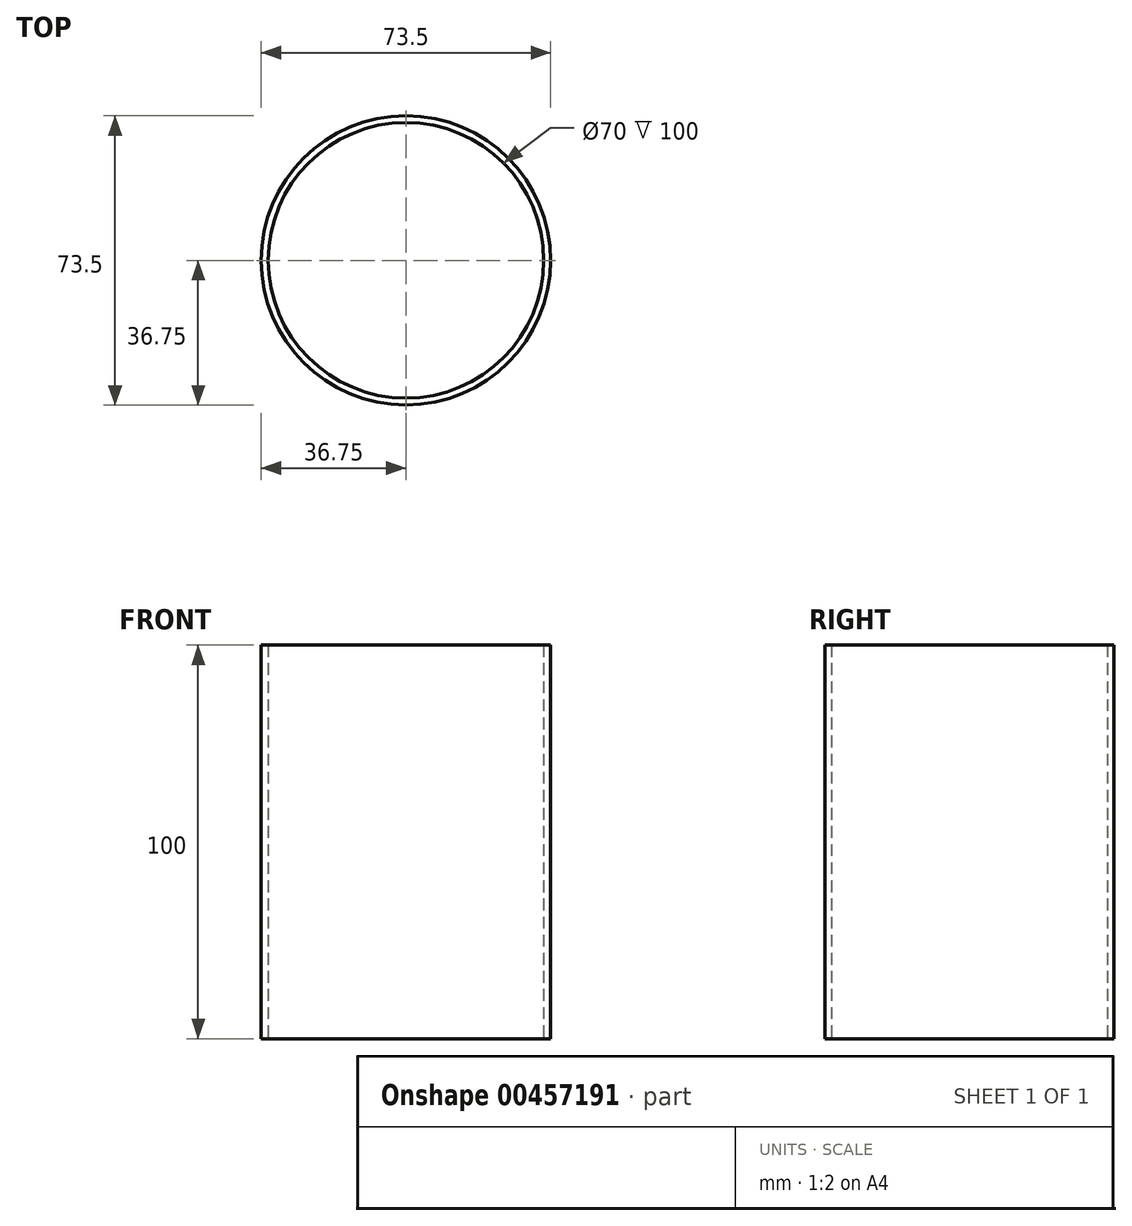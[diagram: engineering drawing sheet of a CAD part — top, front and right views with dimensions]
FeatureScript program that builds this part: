
annotation { "Feature Type Name" : "Feature", "Feature Type Description" : "" }
export const myFeature = defineFeature(function(context is Context, id is Id, definition is map)
    precondition{}
    {
        {
            var Q0;
            Q0=qCreatedBy(makeId("Top.planeOp"),FACE);
            var sketch = newSketch(context, id + "F0", { "sketchPlane" : qUnion([Q0])});
            skCircle(sketch, "E0", {"center": v(0, 0) * mm, "radius": 36.75 * mm});
            skCircle(sketch, "E1", {"center": v(0, 0) * mm, "radius": 35 * mm});
            skSolve(sketch);
        }
        {
            var Q0;
            Q0 = qSketchRegion(id + "F0", true);
            extrude(context, id + "F1", {"entities" : qUnion([Q0]), "depth" : 100 * mm});
        }
    });
